# Revit family: SD50430U-HNI-FOV&SD50230U-HNI-FOV
name_source: partatom
category: 安全设备
revit_build: Autodesk Revit 2016 (Build: 20150220_1215(x64)
units: mm (PartAtom-declared; Revit-internal decimal feet)

## family parameters
主体 = 面
保持注释方向 = 否
共享 = 否
加载时剪切的空心 = 否
圆形连接件大小 = 使用直径
房间计算点 = 否
零件类型 = 标准

## types (2) — shared parameters
Day/Night = Auto / Color / B/W
FOV material = FOV material
Humidity = Less than 95% RH
Indoor/Outdoor = Outdoor
Lens = 0' - 0 3/16"
Minimum Illumination = 0.05Lux@F1.6(Color)
0.005Lux@F1.6(B/W)
Operating Temperature = -40°C ~ 60°C
Power Consumption = 13W, 23W (Heater on)
Power Supply = AC24V/1.5A(±10%), PoE+(802.3at)
Product Material = Aluminum Alloy
Rotation Desired = 0.00°
Tilt Desired = 0.00°
URL = http://www.dahuasecurity.com
Weight = 2.50 kg
Wide Dynamic Range = 120dB
制造商 = DAHUA
默认高程 = 4' - 0"

## per-type parameters (varying)
| type | Image Sensor | Resolution | 型号 |
| 4MP 30x PTZ Network Camera | OV4689 | 4MP | SD50430U-HNI |
| 2MP 30x Starlight PTZ Network Camera | Sony IMX290 | 1080P | SD50230U-HNI |

note: column(s) folded — value = type name in every type: Product Name
